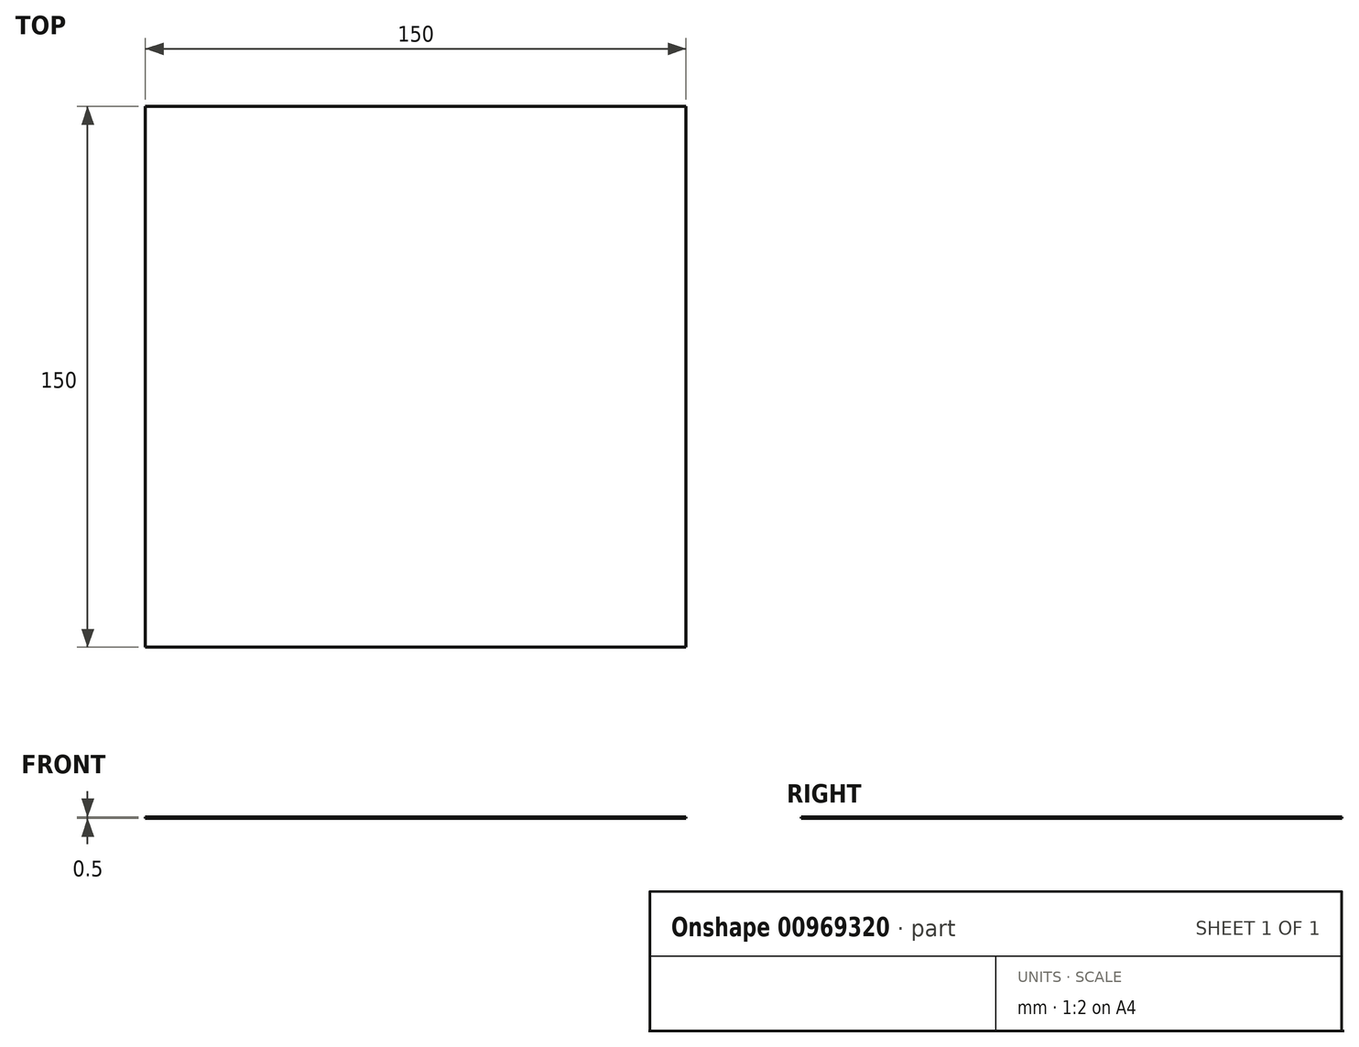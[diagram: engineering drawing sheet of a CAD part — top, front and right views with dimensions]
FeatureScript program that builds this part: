
annotation { "Feature Type Name" : "Feature", "Feature Type Description" : "" }
export const myFeature = defineFeature(function(context is Context, id is Id, definition is map)
    precondition{}
    {
        {
            var Q0;
            Q0=qCreatedBy(makeId("Top.planeOp"),FACE);
            var sketch = newSketch(context, id + "F0", { "sketchPlane" : qUnion([Q0])});
            skLineSegment(sketch, "E0.bottom", {"start": v(75, 75) * mm, "end": v(-75, 75) * mm});
            skLineSegment(sketch, "E0.top", {"start": v(75, -75) * mm, "end": v(-75, -75) * mm});
            skLineSegment(sketch, "E0.left", {"start": v(75, 75) * mm, "end": v(75, -75) * mm});
            skLineSegment(sketch, "E0.right", {"start": v(-75, 75) * mm, "end": v(-75, -75) * mm});
            skPoint(sketch, "E0.middle", {"position": v(0, 0) * mm});
            skSolve(sketch);
        }
        {
            var Q0;
            Q0=makeQuery(id+"F0.imprint","IMPRINT",FACE,{"disambiguationData":[TD([[makeQuery(id+"F0.imprint","IMPRINT",EDGE,{"derivedFrom":sQuery(id+"F0.wireOp",EDGE,"E0.bottom")}),1.0]])]});
            extrude(context, id + "F1", {"entities" : qUnion([Q0]), "depth" : 0.5 * mm, "offsetDistance" : 25 * mm});
        }
    });
